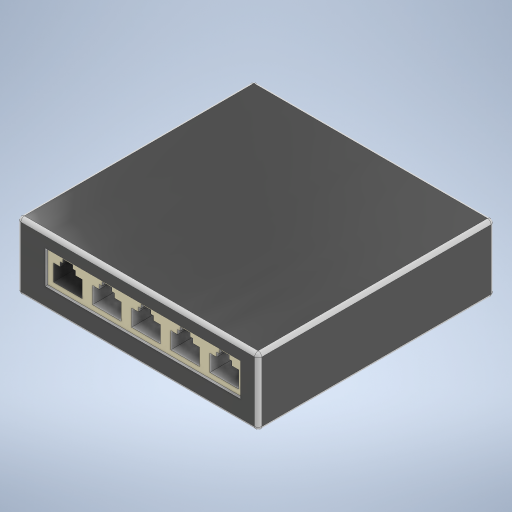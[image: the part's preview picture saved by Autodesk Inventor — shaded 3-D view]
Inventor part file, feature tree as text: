
AUTODESK INVENTOR PART (.ipt)
format: ipt  version: 2023 (Build 270158030, 158C)  size: 320,000 bytes
history: native  units: mm
features: extrude x3, sketch x3, pattern_linear x1, fillet x1
ambient origin geometry x8: Origin, YZ Plane, XZ Plane, XY Plane, X Axis, Y Axis, Z Axis, Center Point
bodies: Solid1 (feature_tree)
feature tree (8):
  extrude  "Extrusion1"  Depth=98.6mm
  extrude  "Extrusion2"  Depth=50.2mm
  extrude  "Extrusion3"  Depth=7.3mm
  pattern_linear  "Rectangular Pattern1"  Spacing1=11.65mm  [1 undecoded]
  fillet  "Fillet1"  Radius=5.8mm
  sketch  "Sketch1"  dims[d0=100.4mm d1=98.6mm]
  sketch  "Sketch2"  dims[d2=49.3mm d3=50.2mm]
  sketch  "Sketch3"  dims[d4=28.1mm d5=0.0mm d6=7.3mm d7=11.65mm d8=5.8mm d9=8.5mm d10=1.08mm d11=0.0mm d12=12.0mm d13=6.35mm d14=4.1mm d15=2.825mm d16=2.825mm d17=1.125mm d18=1.125mm d19=6.95mm d20=1.8mm d21=1.52mm d22=2.15mm d23=2.35mm d24=11.78mm d25=0.0mm d26=50.0mm d28=16.3mm d29=1.5mm]
note: 1 required parameter value undecoded (feature->parameter linkage not recoverable at this tier; creation-order binding heuristic only, values carry confidence <= 0.55)
